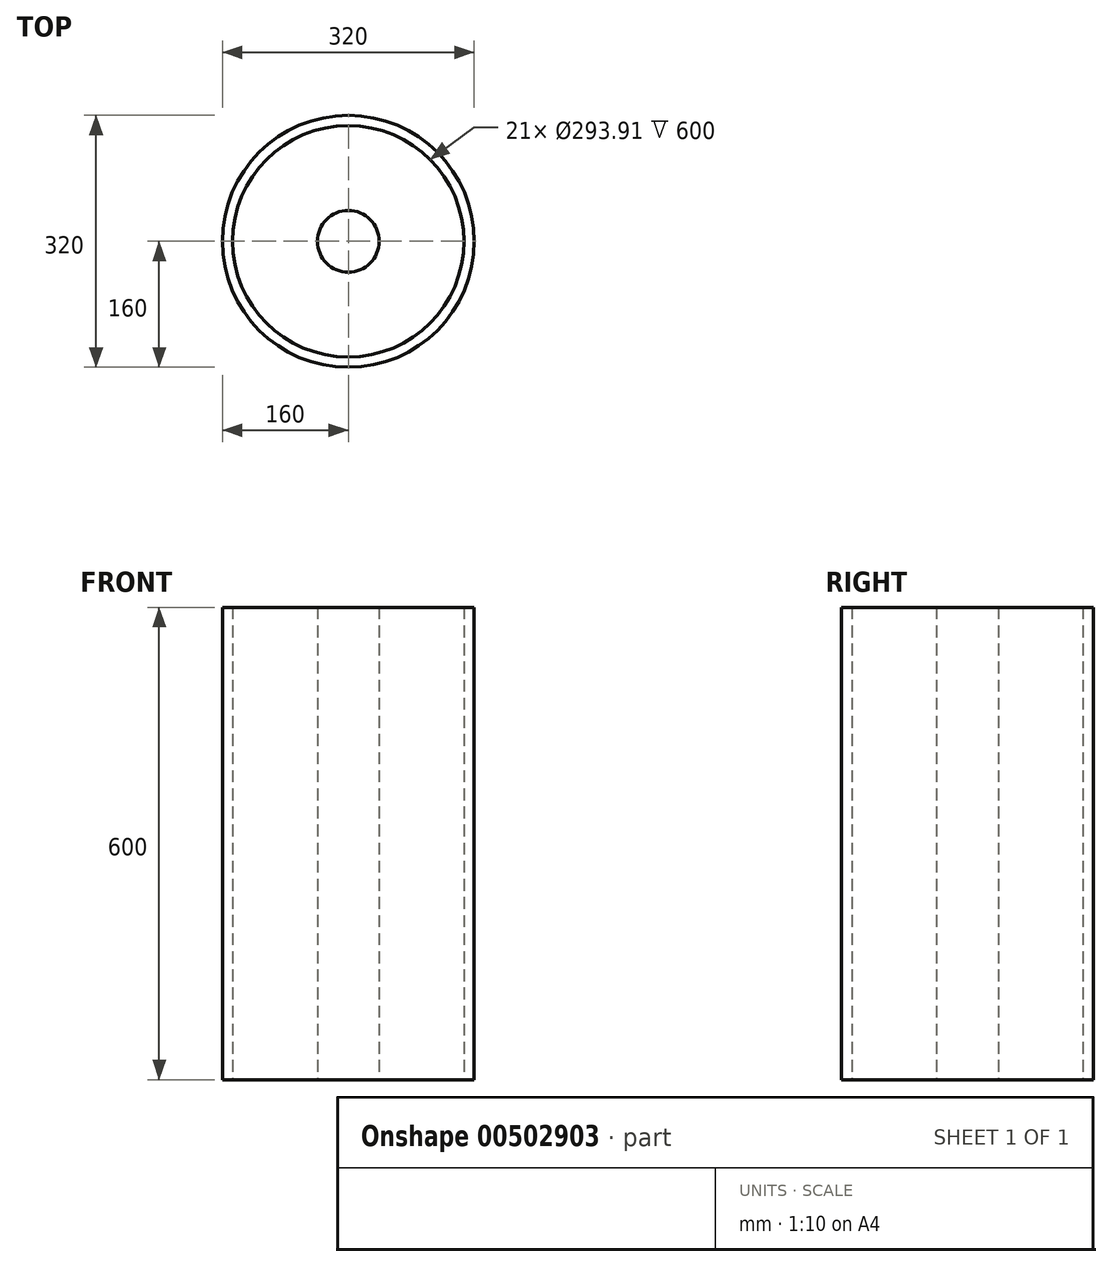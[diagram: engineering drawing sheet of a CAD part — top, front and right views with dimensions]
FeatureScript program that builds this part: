
annotation { "Feature Type Name" : "Feature", "Feature Type Description" : "" }
export const myFeature = defineFeature(function(context is Context, id is Id, definition is map)
    precondition{}
    {
        {
            var Q0;
            Q0=qCreatedBy(makeId("Top.planeOp"),FACE);
            var sketch = newSketch(context, id + "F0", { "sketchPlane" : qUnion([Q0])});
            skCircle(sketch, "E0", {"center": v(0, 0) * mm, "radius": 39.19 * mm});
            skCircle(sketch, "E1", {"center": v(0, 0) * mm, "radius": 146.95 * mm});
            skCircle(sketch, "E2", {"center": v(0, 0) * mm, "radius": 160 * mm});
            skSolve(sketch);
        }
        {
            var Q0;
            Q0=makeQuery(id+"F0.imprint","IMPRINT",FACE,{"disambiguationData":[TD([[makeQuery(id+"F0.imprint","IMPRINT",EDGE,{"derivedFrom":sQuery(id+"F0.wireOp",EDGE,"E0")}),1.0]])]});
            extrude(context, id + "F1", {"entities" : qUnion([Q0]), "depth" : 600 * mm});
        }
        {
            var Q0;
            Q0=qSketchRegion(id+"F0",true);
            extrude(context, id + "F2", {"entities" : qUnion([Q0]), "depth" : 600 * mm});
        }
    });
